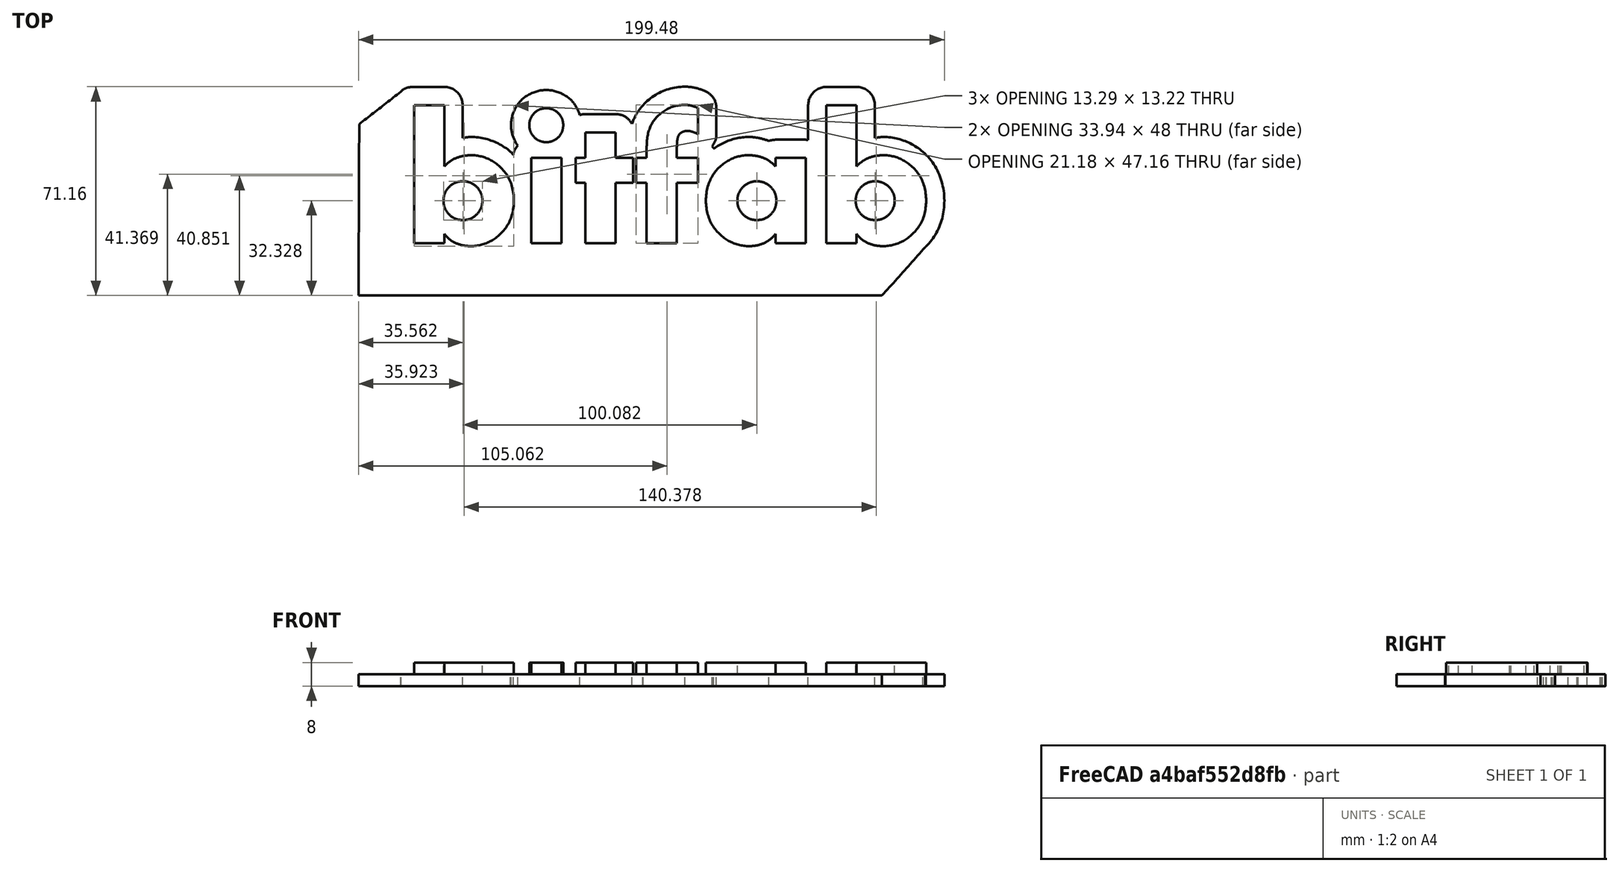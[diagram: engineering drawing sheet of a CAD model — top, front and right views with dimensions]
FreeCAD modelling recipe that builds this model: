
FCSTD DOCUMENT  (FreeCAD 0.16R6706 (Git))
Label: bitfab_3D_logo
License: All rights reserved
LicenseURL: http://en.wikipedia.org/wiki/All_rights_reserved
objects: Part::Feature×12, Part::Extrusion×11, Part::MultiFuse×3, Part::Cut×1, Mesh::Feature×1
note: 27 computed .brp shape members not serialized (recipe doc carries the construction recipe); baked Part::Feature solids carry a one-line shape summary decoded from their .brp

FEATURE [Part::Feature] path4724
  shape: bbox 199.5 x 71.16 x 1.826e-06 mm, 0 faces, 0 solids (baked)
FEATURE [Part::Feature] path4146
  shape: bbox 33.94 x 48 x 1.826e-06 mm, 0 faces, 0 solids (baked)
FEATURE [Part::Feature] path4146001
  shape: bbox 13.29 x 13.22 x 1.826e-06 mm, 0 faces, 0 solids (baked)
FEATURE [Part::Feature] path4148
  shape: bbox 11.56 x 11.56 x 1.826e-06 mm, 0 faces, 0 solids (baked)
FEATURE [Part::Feature] path4148001
  shape: bbox 10.28 x 29.08 x 1.826e-06 mm, 0 faces, 0 solids (baked)
FEATURE [Part::Feature] path4150
  shape: bbox 19.52 x 37.82 x 1.826e-06 mm, 0 faces, 0 solids (baked)
FEATURE [Part::Feature] path4152
  shape: bbox 21.18 x 47.16 x 1.826e-06 mm, 0 faces, 0 solids (baked)
FEATURE [Part::Feature] path4154
  shape: bbox 33.94 x 30.96 x 1.826e-06 mm, 0 faces, 0 solids (baked)
FEATURE [Part::Feature] path4154001
  shape: bbox 13.29 x 13.22 x 1.826e-06 mm, 0 faces, 0 solids (baked)
FEATURE [Part::Feature] path4156
  shape: bbox 33.94 x 48 x 1.826e-06 mm, 0 faces, 0 solids (baked)
FEATURE [Part::Feature] path4156001
  shape: bbox 13.29 x 13.22 x 1.826e-06 mm, 0 faces, 0 solids (baked)
FEATURE [Part::Extrusion] Extrude
  Base = -> path4146
  Dir = (0,0,8)
  Solid = true
FEATURE [Part::Extrusion] Extrude001
  Base = -> path4148
  Dir = (0,0,8)
  Solid = true
FEATURE [Part::Extrusion] Extrude002
  Base = -> path4148001
  Dir = (0,0,8)
  Solid = true
FEATURE [Part::Extrusion] Extrude003
  Base = -> path4150
  Dir = (0,0,8)
  Solid = true
FEATURE [Part::Extrusion] Extrude004
  Base = -> path4152
  Dir = (0,0,8)
  Solid = true
FEATURE [Part::Extrusion] Extrude005
  Base = -> path4154
  Dir = (0,0,8)
  Solid = true
FEATURE [Part::Extrusion] Extrude006
  Base = -> path4156
  Dir = (0,0,8)
  Solid = true
FEATURE [Part::Extrusion] Extrude007
  Base = -> path4146001
  Dir = (0,0,8)
  Solid = true
FEATURE [Part::Extrusion] Extrude008
  Base = -> path4154001
  Dir = (0,0,8)
  Solid = true
FEATURE [Part::Extrusion] Extrude009
  Base = -> path4156001
  Dir = (0,0,8)
  Solid = true
FEATURE [Part::MultiFuse] Fusion  label="letters"
  Shapes = -> [Extrude,Extrude003,Extrude002,Extrude001,Extrude006,Extrude004,Extrude005]
FEATURE [Part::MultiFuse] Fusion001  label="holes"
  Shapes = -> [Extrude007,Extrude009,Extrude008]
FEATURE [Part::Extrusion] Extrude010  label="outline"
  Base = -> path4724
  Dir = (0,0,4)
  Solid = true
FEATURE [Part::Cut] Cut
  Base = -> Fusion
  Tool = -> Fusion001
FEATURE [Part::MultiFuse] Fusion002
  Shapes = -> [Extrude010,Cut]
FEATURE [Part::Feature] Fusion002004  label="Fusion006"
  shape: bbox 199.5 x 71.16 x 8 mm, 165 faces (baked)
FEATURE [Mesh::Feature] Mesh  label="Fusion006 (Meshed)"
